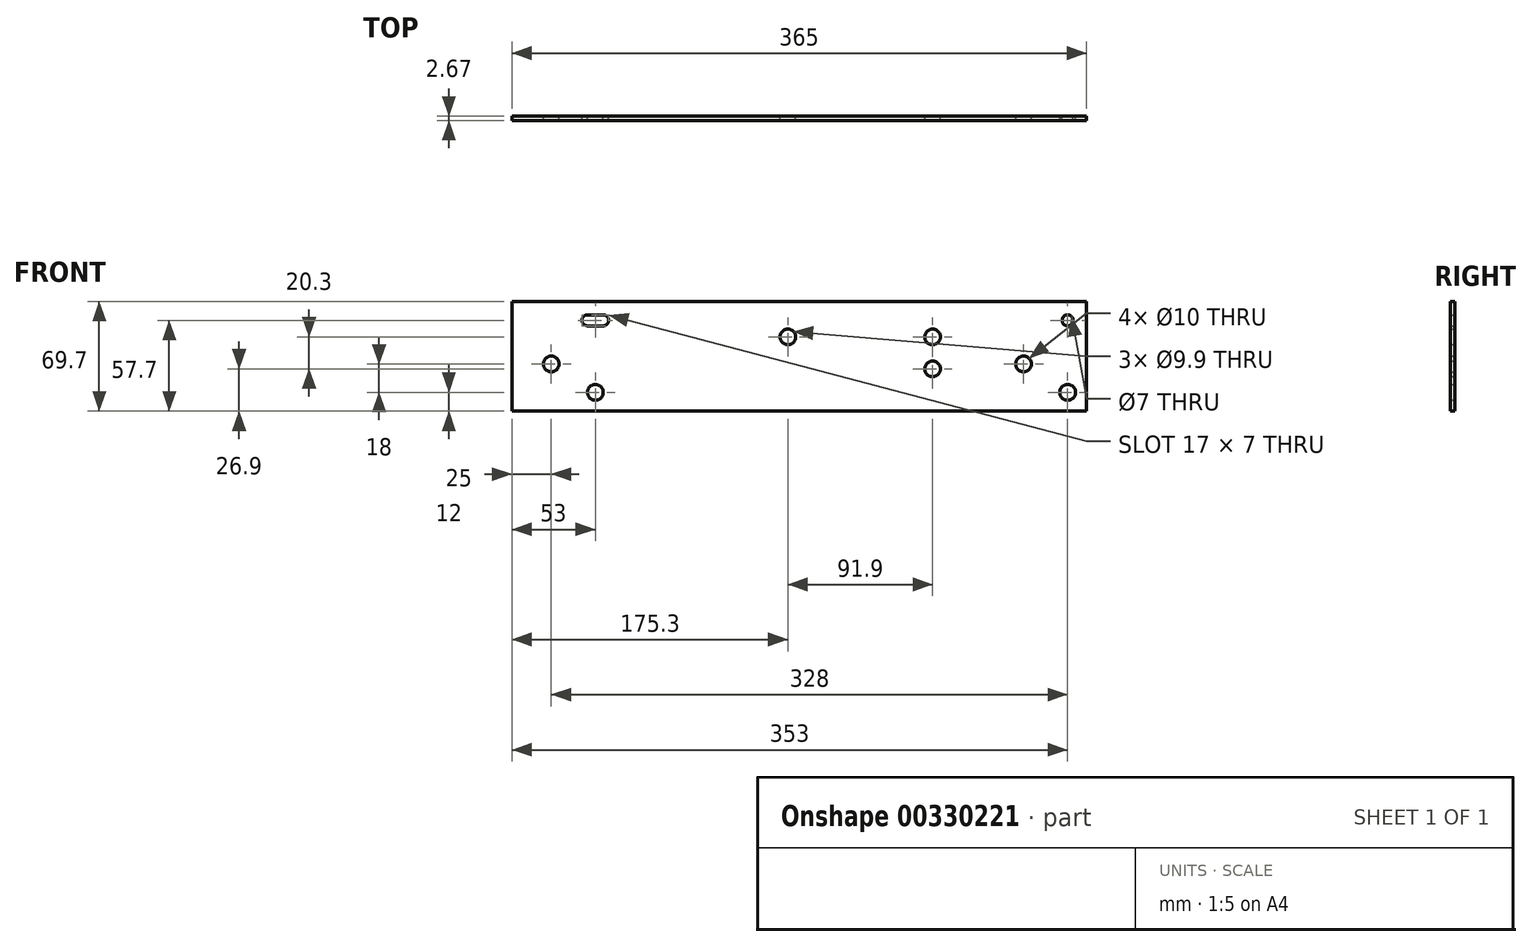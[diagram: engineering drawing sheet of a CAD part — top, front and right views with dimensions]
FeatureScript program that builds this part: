
annotation { "Feature Type Name" : "Feature", "Feature Type Description" : "" }
export const myFeature = defineFeature(function(context is Context, id is Id, definition is map)
    precondition{}
    {
        {
            var Q0;
            Q0=qCreatedBy(makeId("Front.planeOp"),FACE);
            var sketch = newSketch(context, id + "F0", { "sketchPlane" : qUnion([Q0])});
            skLineSegment(sketch, "E0.bottom", {"start": v(0, 0) * mm, "end": v(365, 0) * mm});
            skLineSegment(sketch, "E0.top", {"start": v(0, 69.7) * mm, "end": v(365, 69.7) * mm});
            skLineSegment(sketch, "E0.left", {"start": v(0, 0) * mm, "end": v(0, 69.7) * mm});
            skLineSegment(sketch, "E0.right", {"start": v(365, 0) * mm, "end": v(365, 69.7) * mm});
            skCircle(sketch, "E1", {"center": v(353, 57.7) * mm, "radius": 3.5 * mm});
            skCircle(sketch, "E2", {"center": v(353, 12) * mm, "radius": 5 * mm});
            skCircle(sketch, "E3", {"center": v(267.2, 47.2) * mm, "radius": 4.95 * mm});
            skCircle(sketch, "E4", {"center": v(325, 30) * mm, "radius": 5 * mm});
            skCircle(sketch, "E5", {"center": v(175.3, 47.2) * mm, "radius": 4.95 * mm});
            skCircle(sketch, "E6", {"center": v(25, 30) * mm, "radius": 5 * mm});
            skCircle(sketch, "E7", {"center": v(267.2, 26.9) * mm, "radius": 4.95 * mm});
            skCircle(sketch, "E8", {"center": v(53, 12) * mm, "radius": 5 * mm});
            skLineSegment(sketch, "E9.bottom", {"start": v(48, 61.2) * mm, "end": v(58, 61.2) * mm});
            skLineSegment(sketch, "E9.top", {"start": v(48, 54.2) * mm, "end": v(58, 54.2) * mm});
            skLineSegment(sketch, "E9.left", {"start": v(48, 61.2) * mm, "end": v(48, 54.2) * mm});
            skLineSegment(sketch, "E9.right", {"start": v(58, 61.2) * mm, "end": v(58, 54.2) * mm});
            skCircle(sketch, "E10", {"center": v(58, 57.7) * mm, "radius": 3.5 * mm});
            skCircle(sketch, "E11", {"center": v(48, 57.7) * mm, "radius": 3.5 * mm});
            skSolve(sketch);
        }
        {
            var Q0;
            Q0=qSketchRegion(id+"F0",true);
            var Q1;
            Q1=makeQuery(id+"F0.imprint","IMPRINT",FACE,{"disambiguationData":[TD([[makeQuery(id+"F0.imprint","IMPRINT",EDGE,{"derivedFrom":sQuery(id+"F0.wireOp",EDGE,"E0.bottom")}),1.0]])]});
            extrude(context, id + "F1", {"entities" : qUnion([Q0, Q1]), "depth" : 2.67 * mm});
        }
    });
